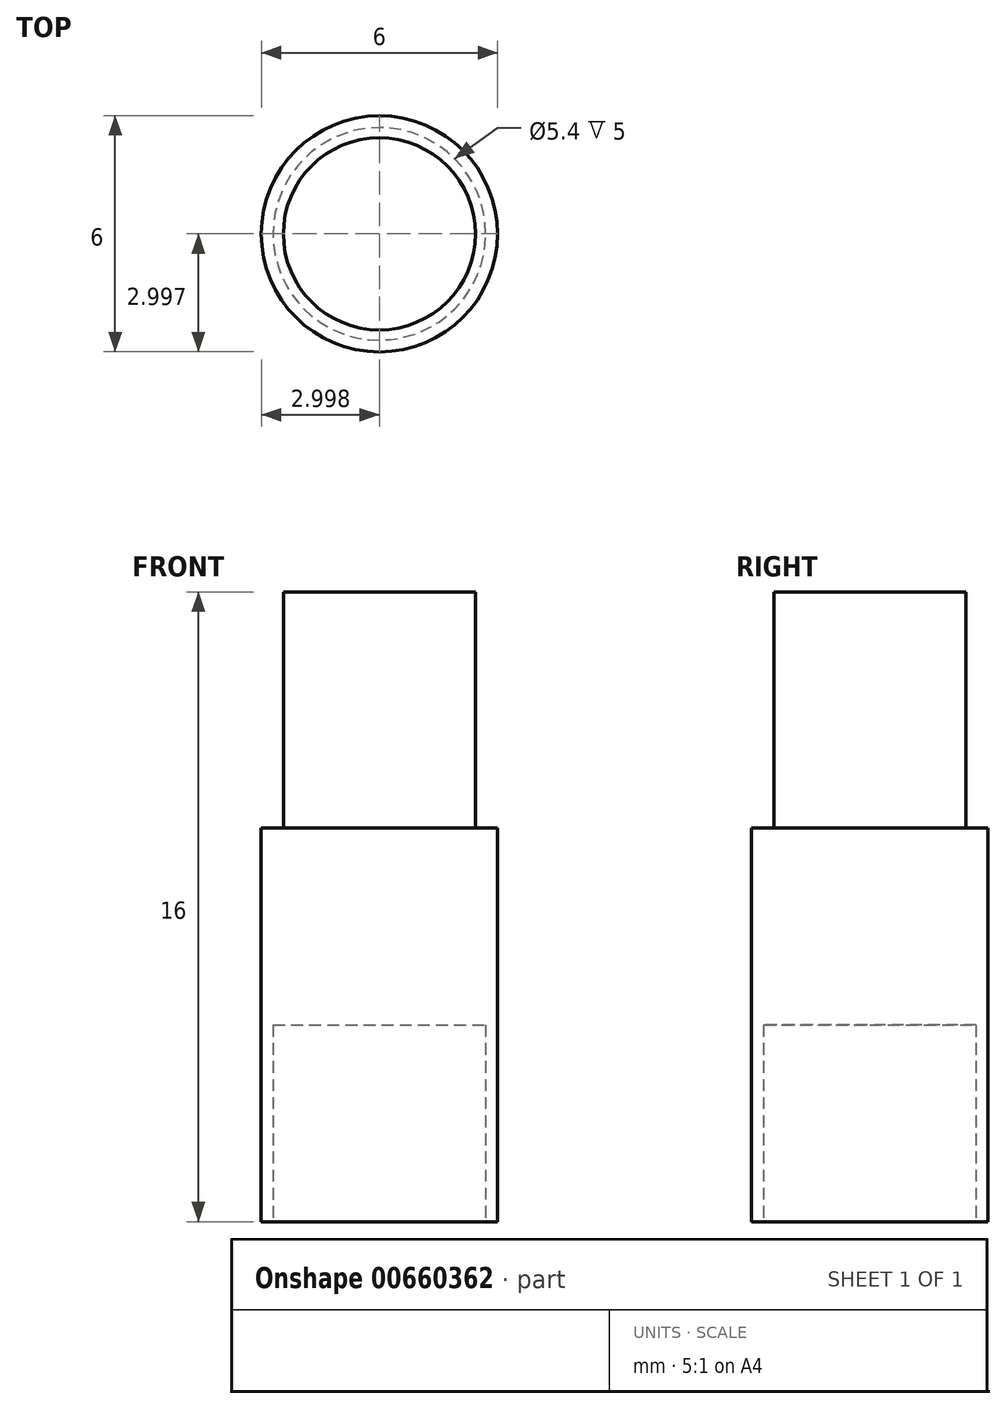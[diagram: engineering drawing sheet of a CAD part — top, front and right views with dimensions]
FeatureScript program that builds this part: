
annotation { "Feature Type Name" : "Feature", "Feature Type Description" : "" }
export const myFeature = defineFeature(function(context is Context, id is Id, definition is map)
    precondition{}
    {
        {
            var Q0;
            Q0=qCreatedBy(makeId("Top.planeOp"),FACE);
            var sketch = newSketch(context, id + "F0", { "sketchPlane" : qUnion([Q0])});
            skCircle(sketch, "E0", {"center": v(-39.5, 19.49) * mm, "radius": 3 * mm});
            skSolve(sketch);
        }
        {
            var Q0;
            Q0=qSketchRegion(id+"F0",true);
            extrude(context, id + "F1", {"entities" : qUnion([Q0]), "depth" : 10 * mm, "offsetDistance" : 25 * mm});
        }
        {
            var Q0;
            Q0=makeQuery(id+"F1.opExtrude","CAP_FACE",FACE,{"disambiguationData":[OSD([sQuery(id+"F0.wireOp",EDGE,"E0")])],"isStart":false});
            var sketch = newSketch(context, id + "F2", { "sketchPlane" : qUnion([Q0])});
            skCircle(sketch, "E1", {"center": v(-39.5, 19.49) * mm, "radius": 2.44 * mm});
            skSolve(sketch);
        }
        {
            var Q0;
            Q0=makeQuery(id+"F2.imprint","IMPRINT",FACE,{"disambiguationData":[TD([[makeQuery(id+"F2.imprint","IMPRINT",EDGE,{"derivedFrom":sQuery(id+"F2.wireOp",EDGE,"E1")}),1.0]])]});
            extrude(context, id + "F3", {"entities" : qUnion([Q0]), "operationType" : NewBodyOperationType.ADD, "depth" : 6 * mm, "offsetDistance" : 25 * mm});
        }
        {
            var Q0;
            Q0=makeQuery(id+"F1.opExtrude","CAP_FACE",FACE,{"disambiguationData":[OSD([sQuery(id+"F0.wireOp",EDGE,"E0")])],"isStart":true});
            var sketch = newSketch(context, id + "F4", { "sketchPlane" : qUnion([Q0])});
            skCircle(sketch, "E2", {"center": v(-39.5, -19.49) * mm, "radius": 2.7 * mm});
            skSolve(sketch);
        }
        {
            var Q0;
            Q0=qSketchRegion(id+"F4",true);
            extrude(context, id + "F5", {"entities" : qUnion([Q0]), "operationType" : NewBodyOperationType.REMOVE, "oppositeDirection" : true, "depth" : 5 * mm, "offsetDistance" : 25 * mm});
        }
    });
